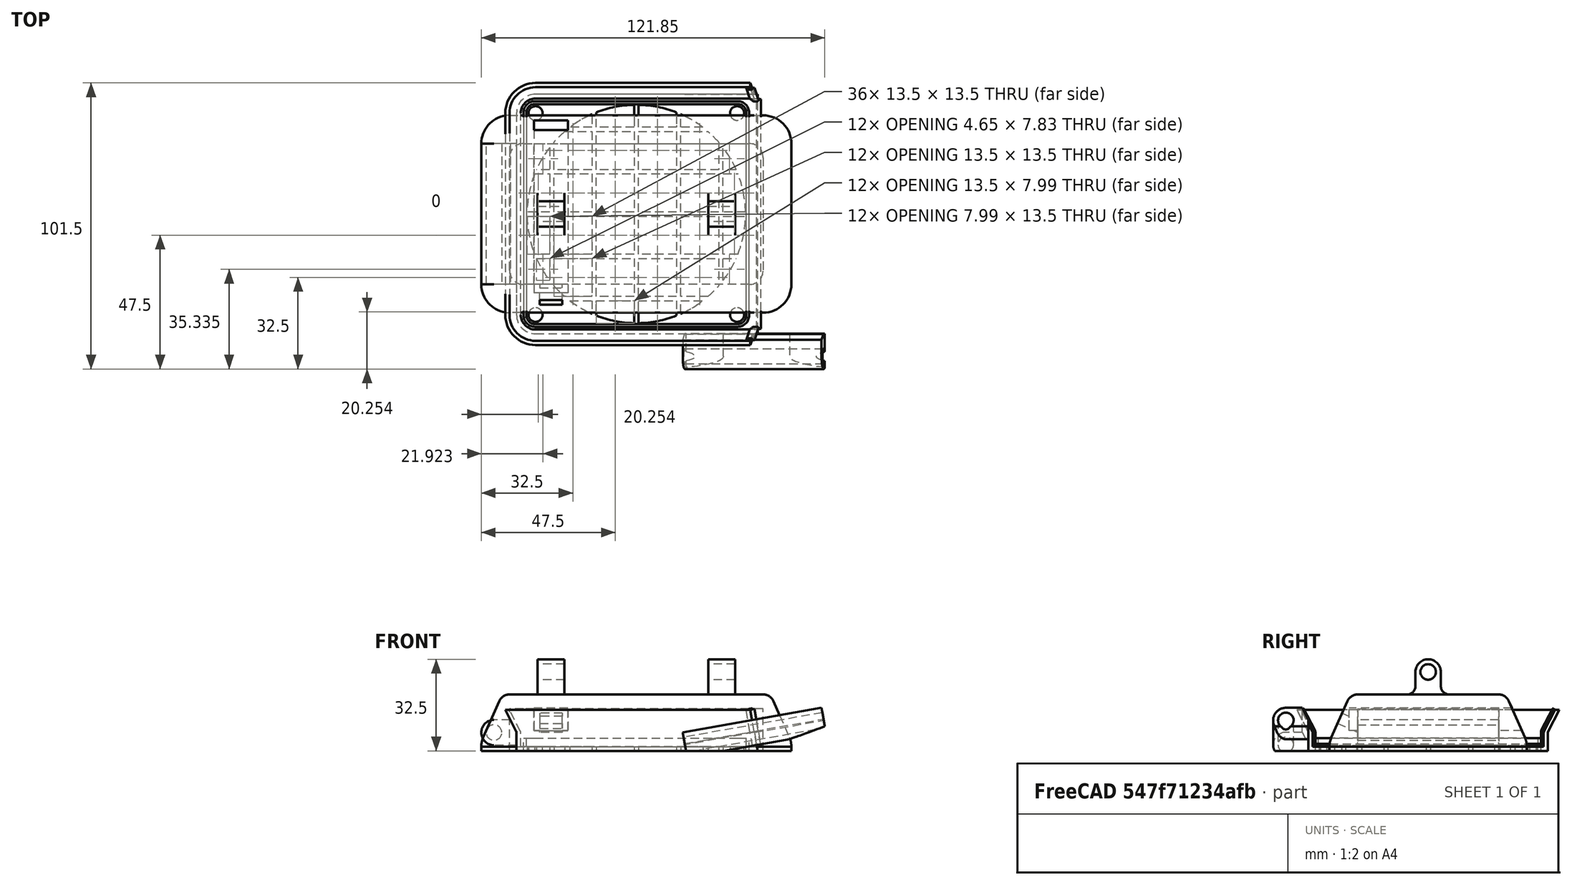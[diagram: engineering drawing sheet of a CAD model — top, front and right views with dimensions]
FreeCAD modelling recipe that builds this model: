
FCSTD DOCUMENT  (FreeCAD 1.0R39285 (Git))
Label: Solder Fume Extractor 2x80mm fans
License: All rights reserved
LicenseURL: https://en.wikipedia.org/wiki/All_rights_reserved
objects: Sketcher::SketchObject×29, PartDesign::Pad×17, PartDesign::CoordinateSystem×13, App::Link×10, PartDesign::Pocket×8, PartDesign::LinearPattern×6, PartDesign::Body×5, PartDesign::AdditivePipe×3, App::DocumentObjectGroup×3, App::FeaturePython×1, Mesh::Feature×1, PartDesign::SubtractivePipe×1, App::Part×1
note: 175 computed .brp shape members not serialized (recipe doc carries the construction recipe); baked Part::Feature solids carry a one-line shape summary decoded from their .brp
EXTERNAL_REF file=Axial Fan.FCStd obj=FanHouse_TopMountHole
EXTERNAL_REF file=Axial Fan.FCStd obj=Assembly

FEATURE [Sketcher::SketchObject] Sketch
  ArcFitTolerance = 1e-06
  AttachmentSupport = -> [XY_Plane]
  FullyConstrained = true
  MakeInternals = false
  MapMode = 5
  sketch-geometry (13):
    g0: LineSegment StartX=-42.5 StartY=35.75 StartZ=0 EndX=-42.5 EndY=-35.75 EndZ=0
    g1: LineSegment StartX=-35.75 StartY=-42.5 StartZ=0 EndX=60 EndY=-42.5 EndZ=0
    g2: LineSegment StartX=60 StartY=-42.5 StartZ=0 EndX=60 EndY=42.5 EndZ=0
    g3: LineSegment StartX=60 StartY=42.5 StartZ=0 EndX=-35.75 EndY=42.5 EndZ=0
    g4: Circle CenterX=-35.75 CenterY=35.75 CenterZ=0 NormalX=0 NormalY=0 NormalZ=1 AngleXU=0 Radius=2.5
    g5: Circle CenterX=35.75 CenterY=35.75 CenterZ=0 NormalX=0 NormalY=0 NormalZ=1 AngleXU=0 Radius=2.5
    g6: Circle CenterX=-35.75 CenterY=-35.75 CenterZ=0 NormalX=0 NormalY=0 NormalZ=1 AngleXU=0 Radius=2.5
    g7: Circle CenterX=35.75 CenterY=-35.75 CenterZ=0 NormalX=0 NormalY=0 NormalZ=1 AngleXU=0 Radius=2.5
    g8: Circle CenterX=0 CenterY=0 CenterZ=0 NormalX=0 NormalY=0 NormalZ=1 AngleXU=0 Radius=38.75
    g9: ArcOfCircle CenterX=-35.75 CenterY=35.75 CenterZ=0 NormalX=0 NormalY=0 NormalZ=1 AngleXU=0 Radius=6.75 StartAngle=1.5708 EndAngle=3.14159
    g10: GeomPoint [constr] X=-42.5 Y=42.5 Z=0
    g11: ArcOfCircle CenterX=-35.75 CenterY=-35.75 CenterZ=0 NormalX=0 NormalY=0 NormalZ=1 AngleXU=0 Radius=6.75 StartAngle=3.14159 EndAngle=4.71239
    g12: GeomPoint [constr] X=-42.5 Y=-42.5 Z=0
  constraints (30):
    c: Coincident(g1,g2)
    c: Coincident(g2,g3)
    c: Vertical(g2)
    c: Horizontal(g1)
    c: Horizontal(g3)
    c: DistanceY(g12,g10) = 85
    c: Equal(g7,g5)
    c: Equal(g5,g4)
    c: Equal(g4,g6)
    c: Diameter(g7) = 5
    c: Symmetric(g7,g5,g-1)
    c: Symmetric(g5,g4,g-2)
    c: Vertical(g6,g4)
    c: Horizontal(g6,g7)
    c: DistanceX(g4,g5) = 71.5
    c: DistanceY(g6,g4) = 71.5
    c: Symmetric(g12,g10,g-1)
    c: Coincident(g8,g-1)
    c: Diameter(g8) = 77.5
    c: DistanceX(g10,g-1) = 42.5
    c: DistanceX(g1) = 60
    c: PointOnObject(g10,g0)
    c: PointOnObject(g10,g3)
    c: Tangent(g0,g9) = -1.5708
    c: Tangent(g3,g9) = -1.5708
    c: PointOnObject(g12,g1)
    c: Tangent(g0,g11) = -1.5708
    c: Tangent(g1,g11) = -1.5708
    c: Equal(g11,g9)
    c: Coincident(g9,g4)
FEATURE [PartDesign::Pad] Pad
  Direction = (0,0,1)
  Length = 1.5
  Length2 = 10
  Profile = -> Sketch
  ReferenceAxis = -> Sketch [N_Axis]
  Refine = true
  Suppressed = false
  Type = 0
FEATURE [Sketcher::SketchObject] Sketch001
  ArcFitTolerance = 1e-06
  AttachmentSupport = -> [Pad]
  ExternalGeometry = -> [Pad]
  FullyConstrained = true
  MakeInternals = false
  MapMode = 5
  Placement = pos=(0,0,1.5) rot=(0,0,1;0rad)
  sketch-geometry (12):
    g0: LineSegment StartX=60 StartY=42.5 StartZ=0 EndX=-35.75 EndY=42.5 EndZ=0
    g1: LineSegment StartX=-42.5 StartY=35.75 StartZ=0 EndX=-42.5 EndY=-35.75 EndZ=0
    g2: LineSegment StartX=-35.75 StartY=-42.5 StartZ=0 EndX=60 EndY=-42.5 EndZ=0
    g3: ArcOfCircle CenterX=-35.75 CenterY=-35.75 CenterZ=0 NormalX=0 NormalY=0 NormalZ=1 AngleXU=0 Radius=6.75 StartAngle=3.14159 EndAngle=4.71239
    g4: ArcOfCircle CenterX=-35.75 CenterY=35.75 CenterZ=0 NormalX=0 NormalY=0 NormalZ=1 AngleXU=0 Radius=6.75 StartAngle=1.5708 EndAngle=3.14159
    g5: LineSegment StartX=60 StartY=-42.5 StartZ=0 EndX=60 EndY=-41 EndZ=0
    g6: LineSegment StartX=60 StartY=-41 StartZ=0 EndX=-35.75 EndY=-41 EndZ=0
    g7: LineSegment StartX=-41 StartY=-35.75 StartZ=0 EndX=-41 EndY=35.75 EndZ=0
    g8: LineSegment StartX=-35.75 StartY=41 StartZ=0 EndX=60 EndY=41 EndZ=0
    g9: LineSegment StartX=60 StartY=41 StartZ=0 EndX=60 EndY=42.5 EndZ=0
    g10: ArcOfCircle CenterX=-35.75 CenterY=-35.75 CenterZ=0 NormalX=0 NormalY=0 NormalZ=1 AngleXU=0 Radius=5.25 StartAngle=3.14159 EndAngle=4.71239
    g11: ArcOfCircle CenterX=-35.75 CenterY=35.75 CenterZ=0 NormalX=0 NormalY=0 NormalZ=1 AngleXU=0 Radius=5.25 StartAngle=1.5708 EndAngle=3.14159
  constraints (30):
    c: Coincident(g0,g-3)
    c: Coincident(g0,g-4)
    c: Horizontal(g2)
    c: Symmetric(g2,g0,g-1)
    c: Equal(g2,g0)
    c: Coincident(g-5,g1)
    c: Coincident(g1,g-5)
    c: Coincident(g3,g2)
    c: Coincident(g3,g1)
    c: Coincident(g4,g1)
    c: Coincident(g4,g0)
    c: Equal(g4,g-4)
    c: Equal(g-4,g3)
    c: Coincident(g5,g2)
    c: Vertical(g5)
    c: Coincident(g6,g5)
    c: Horizontal(g6)
    c: Vertical(g7)
    c: Coincident(g9,g8)
    c: Coincident(g9,g0)
    c: Horizontal(g8)
    c: Vertical(g9)
    c: Equal(g5,g9)
    c: Equal(g6,g8)
    c: Tangent(g10,g6) = 1.5708
    c: Tangent(g10,g7) = 1.5708
    c: Tangent(g11,g7) = 1.5708
    c: Tangent(g11,g8) = 1.5708
    c: DistanceY(g5,g5) = 1.5
    c: Coincident(g11,g4)
FEATURE [PartDesign::Pad] Pad001
  BaseFeature = -> Pad
  Direction = (0,0,1)
  Length = 5
  Length2 = 10
  Profile = -> Sketch001
  ReferenceAxis = -> Sketch001 [N_Axis]
  Refine = true
  Suppressed = false
  Type = 0
FEATURE [Sketcher::SketchObject] Sketch002
  ArcFitTolerance = 1e-06
  AttachmentSupport = -> [Pad001]
  ExternalGeometry = -> [Pad001]
  FullyConstrained = true
  MakeInternals = false
  MapMode = 5
  Placement = pos=(60,0,0) rot=(0.57735,0.57735,0.57735;2.0944rad)
  sketch-geometry (6):
    g0: LineSegment StartX=41.1112 StartY=6.9583 StartZ=0 EndX=45 EndY=14.5 EndZ=0
    g1: LineSegment StartX=45 StartY=14.5 StartZ=0 EndX=46.5 EndY=14.5 EndZ=0
    g2: LineSegment StartX=46.5 StartY=14.5 StartZ=0 EndX=42.6112 EndY=6.9583 EndZ=0
    g3: ArcOfCircle CenterX=43.5 CenterY=6.5 CenterZ=0 NormalX=0 NormalY=0 NormalZ=1 AngleXU=0 Radius=1 StartAngle=2.66551 EndAngle=3.14159
    g4: ArcOfCircle CenterX=42 CenterY=6.5 CenterZ=0 NormalX=0 NormalY=0 NormalZ=1 AngleXU=0 Radius=1 StartAngle=2.66551 EndAngle=3.14159
    g5: LineSegment StartX=42.5 StartY=6.5 StartZ=0 EndX=41 EndY=6.5 EndZ=0
  constraints (16):
    c: Coincident(g0,g1)
    c: Horizontal(g1)
    c: Coincident(g1,g2)
    c: Coincident(g3,g-3)
    c: Coincident(g4,g-3)
    c: Tangent(g4,g0) = 1.5708
    c: Tangent(g3,g2) = -1.5708
    c: Coincident(g5,g3)
    c: Coincident(g5,g4)
    c: Perpendicular(g3,g5)
    c: Perpendicular(g4,g5)
    c: Equal(g1,g5)
    c: Radius(g4) = 1
    c: DistanceY(g3,g1) = 8
    c: DistanceX(g3,g1) = 4
    c: Equal(g4,g3)
FEATURE [PartDesign::AdditivePipe] AdditivePipe
  AuxilleryCurvelinear = true
  AuxillerySpineTangent = false
  BaseFeature = -> Pad001
  Binormal = (0,0,0)
  Mode = 0
  Profile = -> Sketch002
  Refine = true
  Spine = -> Pad001 [Edge32,Edge33,Edge34,Edge35,Edge36]
  SpineTangent = false
  Suppressed = false
  Transformation = 0
  Transition = 0
FEATURE [Sketcher::SketchObject] Sketch003
  ArcFitTolerance = 1e-06
  AttachmentSupport = -> [XY_Plane]
  ExternalGeometry = -> [AdditivePipe]
  FullyConstrained = true
  MakeInternals = false
  MapMode = 5
  sketch-geometry (5):
    g0: LineSegment StartX=-30.75 StartY=42.5 StartZ=0 EndX=-30.75 EndY=-42.5 EndZ=0
    g1: LineSegment StartX=-30.75 StartY=-42.5 StartZ=0 EndX=-29.25 EndY=-42.5 EndZ=0
    g2: LineSegment StartX=-29.25 StartY=-42.5 StartZ=0 EndX=-29.25 EndY=42.5 EndZ=0
    g3: LineSegment StartX=-29.25 StartY=42.5 StartZ=0 EndX=-30.75 EndY=42.5 EndZ=0
    g4: GeomPoint [constr] X=-30 Y=0 Z=0
  constraints (13):
    c: Coincident(g0,g1)
    c: Coincident(g1,g2)
    c: Coincident(g2,g3)
    c: Coincident(g3,g0)
    c: Vertical(g0)
    c: Vertical(g2)
    c: Horizontal(g1)
    c: Horizontal(g3)
    c: Symmetric(g2,g0,g4)
    c: PointOnObject(g4,g-1)
    c: PointOnObject(g1,g-3)
    c: DistanceX(g3,g3) = 1.5
    c: DistanceX(g4,g-1) = 30
FEATURE [PartDesign::Pad] Pad002
  BaseFeature = -> AdditivePipe
  Direction = (0,0,1)
  Length = 10
  Length2 = 10
  Profile = -> Sketch003
  ReferenceAxis = -> Sketch003 [N_Axis]
  Refine = true
  Suppressed = false
  Type = 3
  UpToFace = -> AdditivePipe [Face2]
FEATURE [PartDesign::LinearPattern] LinearPattern
  BaseFeature = -> Pad002
  Direction = -> Sketch003 [H_Axis]
  Length = 60
  Mode = 0
  Occurrences = 5
  Offset = 15
  Originals = -> [Pad002]
  Refine = true
  Suppressed = false
  TransformMode = 0
FEATURE [Sketcher::SketchObject] Sketch004
  ArcFitTolerance = 1e-06
  AttachmentSupport = -> [XY_Plane]
  ExternalGeometry = -> [LinearPattern]
  FullyConstrained = true
  MakeInternals = false
  MapMode = 5
  sketch-geometry (5):
    g0: LineSegment StartX=42.5 StartY=29.25 StartZ=0 EndX=42.5 EndY=30.75 EndZ=0
    g1: LineSegment StartX=42.5 StartY=30.75 StartZ=0 EndX=-42.5 EndY=30.75 EndZ=0
    g2: LineSegment StartX=-42.5 StartY=30.75 StartZ=0 EndX=-42.5 EndY=29.25 EndZ=0
    g3: LineSegment StartX=-42.5 StartY=29.25 StartZ=0 EndX=42.5 EndY=29.25 EndZ=0
    g4: GeomPoint [constr] X=0 Y=30 Z=0
  constraints (13):
    c: Coincident(g0,g1)
    c: Coincident(g1,g2)
    c: Coincident(g2,g3)
    c: Coincident(g3,g0)
    c: Vertical(g0)
    c: Vertical(g2)
    c: Horizontal(g1)
    c: Horizontal(g3)
    c: Symmetric(g2,g0,g4)
    c: PointOnObject(g4,g-2)
    c: PointOnObject(g1,g-3)
    c: DistanceY(g4) = 30
    c: DistanceY(g0,g0) = 1.5
FEATURE [PartDesign::Pad] Pad003
  BaseFeature = -> LinearPattern
  Direction = (0,0,1)
  Length = 10
  Length2 = 10
  Profile = -> Sketch004
  ReferenceAxis = -> Sketch004 [N_Axis]
  Refine = true
  Suppressed = false
  Type = 3
  UpToFace = -> LinearPattern [Face31]
FEATURE [PartDesign::LinearPattern] LinearPattern001
  BaseFeature = -> Pad003
  Direction = -> Sketch004 [V_Axis]
  Length = 60
  Mode = 0
  Occurrences = 5
  Offset = 15
  Originals = -> [Pad003]
  Refine = true
  Reversed = true
  Suppressed = false
  TransformMode = 0
FEATURE [PartDesign::CoordinateSystem] FanMountHole
  AttacherType = Attacher::AttachEngine3D
  AttachmentSupport = -> [LinearPattern001]
  MapMode = 11
  Placement = pos=(-35.75,-35.75,0) rot=(0,0,1;1.5708rad)
FEATURE [PartDesign::CoordinateSystem] LCS_Origin
  AttacherType = Attacher::AttachEngine3D
  AttachmentSupport = -> [X_Axis001]
  MapMode = 2
FEATURE [App::DocumentObjectGroup] Constraints
FEATURE [App::FeaturePython] Variables  # WARN: FeaturePython — macro-defined, semantics opaque (R4)
  Type = App::PropertyContainer
FEATURE [App::DocumentObjectGroup] Configurations
FEATURE [Sketcher::SketchObject] Sketch005
  ArcFitTolerance = 1e-06
  AttachmentSupport = -> [XZ_Plane]
  ExternalGeometry = -> [LinearPattern001]
  FullyConstrained = true
  MakeInternals = false
  MapMode = 5
  Placement = pos=(0,0,0) rot=(1,0,0;1.5708rad)
  sketch-geometry (4):
    g0: LineSegment StartX=60 StartY=14.5 StartZ=0 EndX=60 EndY=0 EndZ=0
    g1: LineSegment StartX=60 StartY=0 StartZ=0 EndX=43 EndY=0 EndZ=0
    g2: LineSegment StartX=43 StartY=0 StartZ=0 EndX=40.4433 EndY=14.5 EndZ=0
    g3: LineSegment StartX=40.4433 StartY=14.5 StartZ=0 EndX=60 EndY=14.5 EndZ=0
  constraints (11):
    c: Coincident(g-3,g0)
    c: PointOnObject(g0,g-1)
    c: Vertical(g0)
    c: Coincident(g0,g1)
    c: PointOnObject(g1,g-1)
    c: Coincident(g1,g2)
    c: PointOnObject(g2,g-3)
    c: Coincident(g2,g3)
    c: Coincident(g3,g0)
    c: DistanceX(g-1,g1) = 43
    c: Angle(g1,g2) = 1.74533
FEATURE [PartDesign::Pocket] Pocket
  BaseFeature = -> LinearPattern001
  Direction = (0,1,-2e-16)
  Length = 5
  Length2 = 5
  Midplane = true
  Profile = -> Sketch005
  ReferenceAxis = -> Sketch005 [N_Axis]
  Refine = true
  Suppressed = false
  Type = 1
FEATURE [PartDesign::CoordinateSystem] OtherFanHolder
  AttacherType = Attacher::AttachEngine3D
  AttachmentSupport = -> [Pocket]
  MapMode = 45
  Placement = pos=(42.8701,0,0.736527) rot=(0.642788,0,0.766044;3.14159rad)
FEATURE [PartDesign::CoordinateSystem] FilterHolderMount
  AttacherType = Attacher::AttachEngine3D
  AttachmentSupport = -> [Pocket]
  MapMode = 11
  Placement = pos=(-35.75,35.75,1.5) rot=(0,0,1;1.5708rad)
FEATURE [Sketcher::SketchObject] Sketch006
  ArcFitTolerance = 1e-06
  AttachmentSupport = -> [XY_Plane002]
  FullyConstrained = true
  MakeInternals = false
  MapMode = 5
  sketch-geometry (15):
    g0: LineSegment StartX=40 StartY=-36 StartZ=0 EndX=40 EndY=36 EndZ=0
    g1: LineSegment StartX=36 StartY=40 StartZ=0 EndX=-36 EndY=40 EndZ=0
    g2: LineSegment StartX=-40 StartY=36 StartZ=0 EndX=-40 EndY=-36 EndZ=0
    g3: LineSegment StartX=-36 StartY=-40 StartZ=0 EndX=36 EndY=-40 EndZ=0
    g4: ArcOfCircle CenterX=36 CenterY=-36 CenterZ=0 NormalX=0 NormalY=0 NormalZ=1 AngleXU=0 Radius=4 StartAngle=4.71239 EndAngle=6.28319
    g5: ArcOfCircle CenterX=36 CenterY=36 CenterZ=0 NormalX=0 NormalY=0 NormalZ=1 AngleXU=0 Radius=4 StartAngle=2e-16 EndAngle=1.5708
    g6: ArcOfCircle CenterX=-36 CenterY=36 CenterZ=0 NormalX=0 NormalY=0 NormalZ=1 AngleXU=0 Radius=4 StartAngle=1.5708 EndAngle=3.14159
    g7: ArcOfCircle CenterX=-36 CenterY=-36 CenterZ=0 NormalX=0 NormalY=0 NormalZ=1 AngleXU=0 Radius=4 StartAngle=3.14159 EndAngle=4.71239
    g8: GeomPoint [constr] X=40 Y=-40 Z=0
    g9: GeomPoint [constr] X=-40 Y=40 Z=0
    g10: Circle CenterX=-35.75 CenterY=35.75 CenterZ=0 NormalX=0 NormalY=0 NormalZ=1 AngleXU=0 Radius=2.5
    g11: Circle CenterX=35.75 CenterY=35.75 CenterZ=0 NormalX=0 NormalY=0 NormalZ=1 AngleXU=0 Radius=2.5
    g12: Circle CenterX=35.75 CenterY=-35.75 CenterZ=0 NormalX=0 NormalY=0 NormalZ=1 AngleXU=0 Radius=2.5
    g13: Circle CenterX=-35.75 CenterY=-35.75 CenterZ=0 NormalX=0 NormalY=0 NormalZ=1 AngleXU=0 Radius=2.5
    g14: Circle CenterX=0 CenterY=0 CenterZ=0 NormalX=0 NormalY=0 NormalZ=1 AngleXU=0 Radius=38.75
  constraints (34):
    c: Tangent(g0,g4) = -1.5708
    c: Tangent(g0,g5) = -1.5708
    c: Tangent(g1,g5) = -1.5708
    c: Tangent(g1,g6) = -1.5708
    c: Tangent(g2,g6) = -1.5708
    c: Tangent(g2,g7) = -1.5708
    c: Tangent(g3,g7) = -1.5708
    c: Tangent(g3,g4) = -1.5708
    c: Vertical(g2)
    c: Horizontal(g1)
    c: Equal(g4,g5)
    c: Equal(g5,g6)
    c: Equal(g6,g7)
    c: PointOnObject(g8,g0)
    c: PointOnObject(g8,g3)
    c: PointOnObject(g9,g1)
    c: PointOnObject(g9,g2)
    c: Radius(g7) = 4
    c: Symmetric(g3,g3,g-2)
    c: Symmetric(g0,g0,g-1)
    c: Equal(g0,g3)
    c: DistanceY(g3,g1) = 80
    c: Equal(g10,g11)
    c: Equal(g11,g12)
    c: Equal(g12,g13)
    c: Symmetric(g10,g11,g-2)
    c: Symmetric(g11,g12,g-1)
    c: Horizontal(g12,g13)
    c: Vertical(g13,g10)
    c: DistanceY(g13,g10) = 71.5
    c: DistanceX(g10,g11) = 71.5
    c: Diameter(g11) = 5
    c: Coincident(g14,g-1)
    c: Diameter(g14) = 77.5
FEATURE [PartDesign::Pad] Pad004
  Direction = (0,0,1)
  Length = 1.5
  Length2 = 10
  Profile = -> Sketch006
  ReferenceAxis = -> Sketch006 [N_Axis]
  Refine = true
  Suppressed = false
  Type = 0
FEATURE [Sketcher::SketchObject] Sketch007
  ArcFitTolerance = 1e-06
  AttachmentSupport = -> [XY_Plane002]
  ExternalGeometry = -> [Pad004]
  FullyConstrained = true
  MakeInternals = false
  MapMode = 5
  sketch-geometry (5):
    g0: LineSegment StartX=-29.25 StartY=-40 StartZ=0 EndX=-29.25 EndY=40 EndZ=0
    g1: LineSegment StartX=-29.25 StartY=40 StartZ=0 EndX=-30.75 EndY=40 EndZ=0
    g2: LineSegment StartX=-30.75 StartY=40 StartZ=0 EndX=-30.75 EndY=-40 EndZ=0
    g3: LineSegment StartX=-30.75 StartY=-40 StartZ=0 EndX=-29.25 EndY=-40 EndZ=0
    g4: GeomPoint [constr] X=-30 Y=0 Z=0
  constraints (13):
    c: Coincident(g0,g1)
    c: Coincident(g1,g2)
    c: Coincident(g2,g3)
    c: Coincident(g3,g0)
    c: Vertical(g0)
    c: Vertical(g2)
    c: Horizontal(g1)
    c: Horizontal(g3)
    c: Symmetric(g2,g0,g4)
    c: PointOnObject(g4,g-1)
    c: PointOnObject(g1,g-3)
    c: DistanceX(g4,g-1) = 30
    c: DistanceX(g1,g1) = 1.5
FEATURE [PartDesign::Pad] Pad005
  BaseFeature = -> Pad004
  Direction = (0,0,1)
  Length = 10
  Length2 = 10
  Profile = -> Sketch007
  ReferenceAxis = -> Sketch007 [N_Axis]
  Refine = true
  Suppressed = false
  Type = 3
  UpToFace = -> Pad004 [Face15]
FEATURE [PartDesign::LinearPattern] LinearPattern002
  BaseFeature = -> Pad005
  Direction = -> Sketch007 [H_Axis]
  Length = 60
  Mode = 0
  Occurrences = 5
  Offset = 15
  Originals = -> [Pad005]
  Refine = true
  Suppressed = false
  TransformMode = 0
FEATURE [Sketcher::SketchObject] Sketch008
  ArcFitTolerance = 1e-06
  AttachmentSupport = -> [XY_Plane002]
  ExternalGeometry = -> [LinearPattern002]
  FullyConstrained = true
  MakeInternals = false
  MapMode = 5
  sketch-geometry (5):
    g0: LineSegment StartX=40 StartY=-30.75 StartZ=0 EndX=40 EndY=-29.25 EndZ=0
    g1: LineSegment StartX=40 StartY=-29.25 StartZ=0 EndX=-40 EndY=-29.25 EndZ=0
    g2: LineSegment StartX=-40 StartY=-29.25 StartZ=0 EndX=-40 EndY=-30.75 EndZ=0
    g3: LineSegment StartX=-40 StartY=-30.75 StartZ=0 EndX=40 EndY=-30.75 EndZ=0
    g4: GeomPoint [constr] X=0 Y=-30 Z=0
  constraints (13):
    c: Coincident(g0,g1)
    c: Coincident(g1,g2)
    c: Coincident(g2,g3)
    c: Coincident(g3,g0)
    c: Vertical(g0)
    c: Vertical(g2)
    c: Horizontal(g1)
    c: Horizontal(g3)
    c: Symmetric(g2,g0,g4)
    c: PointOnObject(g4,g-2)
    c: PointOnObject(g1,g-3)
    c: DistanceY(g4,g-1) = 30
    c: DistanceY(g0,g0) = 1.5
FEATURE [PartDesign::Pad] Pad006
  BaseFeature = -> LinearPattern002
  Direction = (0,0,1)
  Length = 10
  Length2 = 10
  Profile = -> Sketch008
  ReferenceAxis = -> Sketch008 [N_Axis]
  Refine = true
  Suppressed = false
  Type = 3
  UpToFace = -> LinearPattern002 [Face32]
FEATURE [PartDesign::LinearPattern] LinearPattern003
  BaseFeature = -> Pad006
  Direction = -> Sketch008 [V_Axis]
  Length = 60
  Mode = 0
  Occurrences = 5
  Offset = 15
  Originals = -> [Pad006]
  Refine = true
  Suppressed = false
  TransformMode = 0
FEATURE [Sketcher::SketchObject] Sketch009
  ArcFitTolerance = 1e-06
  AttachmentSupport = -> [LinearPattern003]
  ExternalGeometry = -> [LinearPattern003]
  FullyConstrained = true
  MakeInternals = false
  MapMode = 5
  Placement = pos=(0,0,1.5) rot=(0,0,1;0rad)
  sketch-geometry (20):
    g0: LineSegment StartX=-40 StartY=36 StartZ=0 EndX=-40 EndY=-36 EndZ=0
    g1: LineSegment StartX=-36 StartY=-40 StartZ=0 EndX=36 EndY=-40 EndZ=0
    g2: LineSegment StartX=40 StartY=-36 StartZ=0 EndX=40 EndY=36 EndZ=0
    g3: LineSegment StartX=36 StartY=40 StartZ=0 EndX=-36 EndY=40 EndZ=0
    g4: ArcOfCircle CenterX=-36 CenterY=36 CenterZ=0 NormalX=0 NormalY=0 NormalZ=1 AngleXU=0 Radius=4 StartAngle=1.5708 EndAngle=3.14159
    g5: ArcOfCircle CenterX=-36 CenterY=-36 CenterZ=0 NormalX=0 NormalY=0 NormalZ=1 AngleXU=0 Radius=4 StartAngle=3.14159 EndAngle=4.71239
    g6: ArcOfCircle CenterX=36 CenterY=-36 CenterZ=0 NormalX=0 NormalY=0 NormalZ=1 AngleXU=0 Radius=4 StartAngle=4.71239 EndAngle=6.28319
    g7: ArcOfCircle CenterX=36 CenterY=36 CenterZ=0 NormalX=0 NormalY=0 NormalZ=1 AngleXU=0 Radius=4 StartAngle=-9e-16 EndAngle=1.5708
    g8: GeomPoint [constr] X=-40 Y=40 Z=0
    g9: GeomPoint [constr] X=40 Y=-40 Z=0
    g10: LineSegment StartX=-39 StartY=36 StartZ=0 EndX=-39 EndY=-36 EndZ=0
    g11: LineSegment StartX=-36 StartY=-39 StartZ=0 EndX=36 EndY=-39 EndZ=0
    g12: LineSegment StartX=39 StartY=-36 StartZ=0 EndX=39 EndY=36 EndZ=0
    g13: LineSegment StartX=36 StartY=39 StartZ=0 EndX=-36 EndY=39 EndZ=0
    g14: ArcOfCircle CenterX=-36 CenterY=36 CenterZ=0 NormalX=0 NormalY=0 NormalZ=1 AngleXU=0 Radius=3 StartAngle=1.5708 EndAngle=3.14159
    g15: ArcOfCircle CenterX=-36 CenterY=-36 CenterZ=0 NormalX=0 NormalY=0 NormalZ=1 AngleXU=0 Radius=3 StartAngle=3.14159 EndAngle=4.71239
    g16: ArcOfCircle CenterX=36 CenterY=-36 CenterZ=0 NormalX=0 NormalY=0 NormalZ=1 AngleXU=0 Radius=3 StartAngle=4.71239 EndAngle=6.28319
    g17: ArcOfCircle CenterX=36 CenterY=36 CenterZ=0 NormalX=0 NormalY=0 NormalZ=1 AngleXU=0 Radius=3 StartAngle=-9e-16 EndAngle=1.5708
    g18: GeomPoint [constr] X=-39 Y=39 Z=0
    g19: GeomPoint [constr] X=39 Y=-39 Z=0
  constraints (44):
    c: Tangent(g0,g4) = -1.5708
    c: Tangent(g0,g5) = -1.5708
    c: Tangent(g1,g5) = -1.5708
    c: Tangent(g1,g6) = -1.5708
    c: Tangent(g2,g6) = -1.5708
    c: Tangent(g2,g7) = -1.5708
    c: Tangent(g3,g7) = -1.5708
    c: Tangent(g3,g4) = -1.5708
    c: Vertical(g0)
    c: Vertical(g2)
    c: Horizontal(g1)
    c: Equal(g4,g5)
    c: Equal(g5,g6)
    c: Equal(g6,g7)
    c: PointOnObject(g8,g0)
    c: PointOnObject(g8,g3)
    c: PointOnObject(g9,g1)
    c: PointOnObject(g9,g2)
    c: Coincident(g3,g-5)
    c: Equal(g-5,g7)
    c: Coincident(g3,g-3)
    c: Equal(g3,g2)
    c: Tangent(g10,g14) = -1.5708
    c: Tangent(g10,g15) = -1.5708
    c: Tangent(g11,g15) = -1.5708
    c: Tangent(g11,g16) = -1.5708
    c: Tangent(g12,g16) = -1.5708
    c: Tangent(g12,g17) = -1.5708
    c: Tangent(g13,g17) = -1.5708
    c: Tangent(g13,g14) = -1.5708
    c: Vertical(g10)
    c: Horizontal(g11)
    c: Equal(g14,g15)
    c: Equal(g15,g16)
    c: Equal(g16,g17)
    c: PointOnObject(g18,g10)
    c: PointOnObject(g18,g13)
    c: PointOnObject(g19,g11)
    c: PointOnObject(g19,g12)
    c: Symmetric(g12,g12,g-1)
    c: Symmetric(g13,g13,g-2)
    c: Equal(g11,g12)
    c: DistanceX(g12,g2) = 1
    c: Horizontal(g2,g12)
FEATURE [PartDesign::Pad] Pad007
  BaseFeature = -> LinearPattern003
  Direction = (0,0,1)
  Length = 3
  Length2 = 10
  Profile = -> Sketch009
  ReferenceAxis = -> Sketch009 [N_Axis]
  Refine = true
  Suppressed = false
  Type = 0
FEATURE [PartDesign::CoordinateSystem] FanHolder
  AttacherType = Attacher::AttachEngine3D
  AttachmentOffset = pos=(0,0,3) rot=(0,0,1;0rad)
  AttachmentSupport = -> [Pad007]
  MapMode = 11
  Placement = pos=(-35.75,35.75,4.5) rot=(0,0,1;1.5708rad)
FEATURE [PartDesign::Body] Body001  label="FilterHolder"
  AllowCompound = false
  Group = -> [Sketch006,Pad004,Sketch007,Pad005,LinearPattern002,Sketch008,Pad006,LinearPattern003,Sketch009,Pad007,FanHolder]
  Origin = -> Origin002
  Tip = -> Pad007
FEATURE [Sketcher::SketchObject] Sketch010
  ArcFitTolerance = 1e-06
  AttachmentSupport = -> [XZ_Plane]
  ExternalGeometry = -> [Pocket]
  FullyConstrained = true
  MakeInternals = false
  MapMode = 5
  Placement = pos=(0,0,0) rot=(1,0,0;1.5708rad)
  sketch-geometry (7):
    g0: ArcOfCircle CenterX=-43.5 CenterY=6.5 CenterZ=0 NormalX=0 NormalY=0 NormalZ=1 AngleXU=0 Radius=1 StartAngle=-2.4e-14 EndAngle=0.476081
    g1: LineSegment StartX=-42.5 StartY=6.5 StartZ=0 EndX=-42.5 EndY=2 EndZ=0
    g2: LineSegment StartX=-42.5 StartY=2 StartZ=0 EndX=-50.5 EndY=2 EndZ=0
    g3: LineSegment StartX=-42.6112 StartY=6.9583 StartZ=0 EndX=-44.6953 EndY=11 EndZ=0
    g4: LineSegment StartX=-44.6953 StartY=11 StartZ=0 EndX=-50.5 EndY=11 EndZ=0
    g5: ArcOfCircle CenterX=-50.5 CenterY=6.5 CenterZ=0 NormalX=0 NormalY=0 NormalZ=1 AngleXU=0 Radius=4.5 StartAngle=1.5708 EndAngle=4.71239
    g6: Circle CenterX=-50.5 CenterY=6.5 CenterZ=0 NormalX=0 NormalY=0 NormalZ=1 AngleXU=0 Radius=2.75
  constraints (18):
    c: Coincident(g0,g-5)
    c: Coincident(g0,g-5)
    c: Equal(g-5,g0)
    c: Coincident(g1,g0)
    c: PointOnObject(g1,g-3)
    c: Coincident(g2,g1)
    c: Horizontal(g2)
    c: Coincident(g3,g0)
    c: PointOnObject(g3,g-4)
    c: Horizontal(g4)
    c: Tangent(g5,g4) = -1.5708
    c: Tangent(g5,g2) = 1.5708
    c: Diameter(g5) = 9
    c: Diameter(g6) = 5.5
    c: Coincident(g6,g5)
    c: Horizontal(g0,g5)
    c: Coincident(g3,g4)
    c: DistanceX(g5,g-4) = 4
FEATURE [PartDesign::Pad] Pad008
  BaseFeature = -> Pocket
  Direction = (0,-1,2e-16)
  Length = 50
  Length2 = 10
  Midplane = true
  Profile = -> Sketch010
  ReferenceAxis = -> Sketch010 [N_Axis]
  Refine = true
  Suppressed = false
  Type = 0
FEATURE [Sketcher::SketchObject] Sketch011
  ArcFitTolerance = 1e-06
  AttachmentSupport = -> [Pad008]
  ExternalGeometry = -> [Pad008]
  FullyConstrained = true
  MakeInternals = false
  MapMode = 5
  Placement = pos=(41.7034,1.6e-15,7.35343) rot=(0.540716,0.540716,0.6444;1.99673rad)
  sketch-geometry (7):
    g0: ArcOfCircle CenterX=-43.0908 CenterY=-0.761797 CenterZ=0 NormalX=0 NormalY=0 NormalZ=1 AngleXU=0 Radius=0.6 StartAngle=6.10761 EndAngle=6.92787
    g1: LineSegment StartX=-44.66 StartY=3.6334 StartZ=0 EndX=-42.6112 EndY=-0.401229 EndZ=0
    g2: LineSegment StartX=-42.5 StartY=-5.3666 StartZ=0 EndX=-42.5 EndY=-0.866599 EndZ=0
    g3: LineSegment StartX=-42.5 StartY=-5.3666 StartZ=0 EndX=-50.5 EndY=-5.3666 EndZ=0
    g4: LineSegment StartX=-44.66 StartY=3.6334 StartZ=0 EndX=-50.5 EndY=3.6334 EndZ=0
    g5: ArcOfCircle CenterX=-50.5 CenterY=-0.866599 CenterZ=0 NormalX=0 NormalY=0 NormalZ=1 AngleXU=0 Radius=4.5 StartAngle=1.5708 EndAngle=4.71239
    g6: Circle CenterX=-50.5 CenterY=-0.866599 CenterZ=0 NormalX=0 NormalY=0 NormalZ=1 AngleXU=0 Radius=2.75
  constraints (18):
    c: Coincident(g0,g-3)
    c: Coincident(g0,g-4)
    c: Radius(g0) = 0.6
    c: Coincident(g3,g2)
    c: Horizontal(g3)
    c: Coincident(g4,g1)
    c: Horizontal(g4)
    c: Tangent(g5,g4) = -1.5708
    c: Tangent(g5,g3) = 1.5708
    c: Diameter(g5) = 9
    c: Horizontal(g5,g2)
    c: Coincident(g6,g5)
    c: Diameter(g6) = 5.5
    c: DistanceX(g5,g-4) = 4
    c: Coincident(g2,g0)
    c: PointOnObject(g1,g-4)
    c: PointOnObject(g2,g-3)
    c: Coincident(g0,g1)
FEATURE [PartDesign::Pad] Pad009
  BaseFeature = -> Pad008
  Direction = (0.984808,-2e-16,0.173648)
  Length = 50
  Length2 = 10
  Midplane = true
  Profile = -> Sketch011
  ReferenceAxis = -> Sketch011 [N_Axis]
  Refine = true
  Suppressed = false
  Type = 0
FEATURE [Mesh::Feature] base_mount
FEATURE [Sketcher::SketchObject] Sketch014
  ArcFitTolerance = 1e-06
  AttachmentSupport = -> [XY_Plane004]
  FullyConstrained = true
  MakeInternals = false
  MapMode = 5
  sketch-geometry (13):
    g0: LineSegment StartX=-42.5 StartY=35.75 StartZ=0 EndX=-42.5 EndY=-35.75 EndZ=0
    g1: LineSegment StartX=-35.75 StartY=-42.5 StartZ=0 EndX=60 EndY=-42.5 EndZ=0
    g2: LineSegment StartX=60 StartY=-42.5 StartZ=0 EndX=60 EndY=42.5 EndZ=0
    g3: LineSegment StartX=60 StartY=42.5 StartZ=0 EndX=-35.75 EndY=42.5 EndZ=0
    g4: Circle CenterX=-35.75 CenterY=35.75 CenterZ=0 NormalX=0 NormalY=0 NormalZ=1 AngleXU=0 Radius=2.5
    g5: Circle CenterX=35.75 CenterY=35.75 CenterZ=0 NormalX=0 NormalY=0 NormalZ=1 AngleXU=0 Radius=2.5
    g6: Circle CenterX=-35.75 CenterY=-35.75 CenterZ=0 NormalX=0 NormalY=0 NormalZ=1 AngleXU=0 Radius=2.5
    g7: Circle CenterX=35.75 CenterY=-35.75 CenterZ=0 NormalX=0 NormalY=0 NormalZ=1 AngleXU=0 Radius=2.5
    g8: Circle CenterX=0 CenterY=0 CenterZ=0 NormalX=0 NormalY=0 NormalZ=1 AngleXU=0 Radius=38.75
    g9: ArcOfCircle CenterX=-35.75 CenterY=35.75 CenterZ=0 NormalX=0 NormalY=0 NormalZ=1 AngleXU=0 Radius=6.75 StartAngle=1.5708 EndAngle=3.14159
    g10: GeomPoint [constr] X=-42.5 Y=42.5 Z=0
    g11: ArcOfCircle CenterX=-35.75 CenterY=-35.75 CenterZ=0 NormalX=0 NormalY=0 NormalZ=1 AngleXU=0 Radius=6.75 StartAngle=3.14159 EndAngle=4.71239
    g12: GeomPoint [constr] X=-42.5 Y=-42.5 Z=0
  constraints (30):
    c: Coincident(g1,g2)
    c: Coincident(g2,g3)
    c: Vertical(g2)
    c: Horizontal(g1)
    c: Horizontal(g3)
    c: DistanceY(g12,g10) = 85
    c: Equal(g7,g5)
    c: Equal(g5,g4)
    c: Equal(g4,g6)
    c: Diameter(g7) = 5
    c: Symmetric(g7,g5,g-1)
    c: Symmetric(g5,g4,g-2)
    c: Vertical(g6,g4)
    c: Horizontal(g6,g7)
    c: DistanceX(g4,g5) = 71.5
    c: DistanceY(g6,g4) = 71.5
    c: Symmetric(g12,g10,g-1)
    c: Coincident(g8,g-1)
    c: Diameter(g8) = 77.5
    c: DistanceX(g10,g-1) = 42.5
    c: DistanceX(g1) = 60
    c: PointOnObject(g10,g0)
    c: PointOnObject(g10,g3)
    c: Tangent(g0,g9) = -1.5708
    c: Tangent(g3,g9) = -1.5708
    c: PointOnObject(g12,g1)
    c: Tangent(g0,g11) = -1.5708
    c: Tangent(g1,g11) = -1.5708
    c: Equal(g11,g9)
    c: Coincident(g9,g4)
FEATURE [PartDesign::Pad] Pad010
  Direction = (0,0,1)
  Length = 1.5
  Length2 = 10
  Profile = -> Sketch014
  ReferenceAxis = -> Sketch014 [N_Axis]
  Refine = true
  Suppressed = false
  Type = 0
FEATURE [Sketcher::SketchObject] Sketch015
  ArcFitTolerance = 1e-06
  AttachmentSupport = -> [Pad010]
  ExternalGeometry = -> [Pad010]
  FullyConstrained = true
  MakeInternals = false
  MapMode = 5
  Placement = pos=(0,0,1.5) rot=(0,0,1;0rad)
  sketch-geometry (12):
    g0: LineSegment StartX=60 StartY=42.5 StartZ=0 EndX=-35.75 EndY=42.5 EndZ=0
    g1: LineSegment StartX=-42.5 StartY=35.75 StartZ=0 EndX=-42.5 EndY=-35.75 EndZ=0
    g2: LineSegment StartX=-35.75 StartY=-42.5 StartZ=0 EndX=60 EndY=-42.5 EndZ=0
    g3: ArcOfCircle CenterX=-35.75 CenterY=-35.75 CenterZ=0 NormalX=0 NormalY=0 NormalZ=1 AngleXU=0 Radius=6.75 StartAngle=3.14159 EndAngle=4.71239
    g4: ArcOfCircle CenterX=-35.75 CenterY=35.75 CenterZ=0 NormalX=0 NormalY=0 NormalZ=1 AngleXU=0 Radius=6.75 StartAngle=1.5708 EndAngle=3.14159
    g5: LineSegment StartX=60 StartY=-42.5 StartZ=0 EndX=60 EndY=-41 EndZ=0
    g6: LineSegment StartX=60 StartY=-41 StartZ=0 EndX=-35.75 EndY=-41 EndZ=0
    g7: LineSegment StartX=-41 StartY=-35.75 StartZ=0 EndX=-41 EndY=35.75 EndZ=0
    g8: LineSegment StartX=-35.75 StartY=41 StartZ=0 EndX=60 EndY=41 EndZ=0
    g9: LineSegment StartX=60 StartY=41 StartZ=0 EndX=60 EndY=42.5 EndZ=0
    g10: ArcOfCircle CenterX=-35.75 CenterY=-35.75 CenterZ=0 NormalX=0 NormalY=0 NormalZ=1 AngleXU=0 Radius=5.25 StartAngle=3.14159 EndAngle=4.71239
    g11: ArcOfCircle CenterX=-35.75 CenterY=35.75 CenterZ=0 NormalX=0 NormalY=0 NormalZ=1 AngleXU=0 Radius=5.25 StartAngle=1.5708 EndAngle=3.14159
  constraints (30):
    c: Coincident(g0,g-3)
    c: Coincident(g0,g-4)
    c: Horizontal(g2)
    c: Symmetric(g2,g0,g-1)
    c: Equal(g2,g0)
    c: Coincident(g-5,g1)
    c: Coincident(g1,g-5)
    c: Coincident(g3,g2)
    c: Coincident(g3,g1)
    c: Coincident(g4,g1)
    c: Coincident(g4,g0)
    c: Equal(g4,g-4)
    c: Equal(g-4,g3)
    c: Coincident(g5,g2)
    c: Vertical(g5)
    c: Coincident(g6,g5)
    c: Horizontal(g6)
    c: Vertical(g7)
    c: Coincident(g9,g8)
    c: Coincident(g9,g0)
    c: Horizontal(g8)
    c: Vertical(g9)
    c: Equal(g5,g9)
    c: Equal(g6,g8)
    c: Tangent(g10,g6) = 1.5708
    c: Tangent(g10,g7) = 1.5708
    c: Tangent(g11,g7) = 1.5708
    c: Tangent(g11,g8) = 1.5708
    c: DistanceY(g5,g5) = 1.5
    c: Coincident(g11,g4)
FEATURE [PartDesign::Pad] Pad011
  BaseFeature = -> Pad010
  Direction = (0,0,1)
  Length = 5
  Length2 = 10
  Profile = -> Sketch015
  ReferenceAxis = -> Sketch015 [N_Axis]
  Refine = true
  Suppressed = false
  Type = 0
FEATURE [Sketcher::SketchObject] Sketch016
  ArcFitTolerance = 1e-06
  AttachmentSupport = -> [Pad011]
  ExternalGeometry = -> [Pad011]
  FullyConstrained = true
  MakeInternals = false
  MapMode = 5
  Placement = pos=(60,0,0) rot=(0.57735,0.57735,0.57735;2.0944rad)
  sketch-geometry (6):
    g0: LineSegment StartX=41.1112 StartY=6.9583 StartZ=0 EndX=45 EndY=14.5 EndZ=0
    g1: LineSegment StartX=45 StartY=14.5 StartZ=0 EndX=46.5 EndY=14.5 EndZ=0
    g2: LineSegment StartX=46.5 StartY=14.5 StartZ=0 EndX=42.6112 EndY=6.9583 EndZ=0
    g3: ArcOfCircle CenterX=43.5 CenterY=6.5 CenterZ=0 NormalX=0 NormalY=0 NormalZ=1 AngleXU=0 Radius=1 StartAngle=2.66551 EndAngle=3.14159
    g4: ArcOfCircle CenterX=42 CenterY=6.5 CenterZ=0 NormalX=0 NormalY=0 NormalZ=1 AngleXU=0 Radius=1 StartAngle=2.66551 EndAngle=3.14159
    g5: LineSegment StartX=42.5 StartY=6.5 StartZ=0 EndX=41 EndY=6.5 EndZ=0
  constraints (16):
    c: Coincident(g0,g1)
    c: Horizontal(g1)
    c: Coincident(g1,g2)
    c: Coincident(g3,g-3)
    c: Coincident(g4,g-3)
    c: Tangent(g4,g0) = 1.5708
    c: Tangent(g3,g2) = -1.5708
    c: Coincident(g5,g3)
    c: Coincident(g5,g4)
    c: Perpendicular(g3,g5)
    c: Perpendicular(g4,g5)
    c: Equal(g1,g5)
    c: Radius(g4) = 1
    c: DistanceY(g3,g1) = 8
    c: DistanceX(g3,g1) = 4
    c: Equal(g4,g3)
FEATURE [PartDesign::AdditivePipe] AdditivePipe001
  AuxilleryCurvelinear = true
  AuxillerySpineTangent = false
  BaseFeature = -> Pad011
  Binormal = (0,0,0)
  Mode = 0
  Profile = -> Sketch016
  Refine = true
  Spine = -> Pad011 [Edge32,Edge33,Edge34,Edge35,Edge36]
  SpineTangent = false
  Suppressed = false
  Transformation = 0
  Transition = 0
FEATURE [Sketcher::SketchObject] Sketch017
  ArcFitTolerance = 1e-06
  AttachmentSupport = -> [XY_Plane004]
  ExternalGeometry = -> [AdditivePipe001]
  FullyConstrained = true
  MakeInternals = false
  MapMode = 5
  sketch-geometry (5):
    g0: LineSegment StartX=-30.75 StartY=42.5 StartZ=0 EndX=-30.75 EndY=-42.5 EndZ=0
    g1: LineSegment StartX=-30.75 StartY=-42.5 StartZ=0 EndX=-29.25 EndY=-42.5 EndZ=0
    g2: LineSegment StartX=-29.25 StartY=-42.5 StartZ=0 EndX=-29.25 EndY=42.5 EndZ=0
    g3: LineSegment StartX=-29.25 StartY=42.5 StartZ=0 EndX=-30.75 EndY=42.5 EndZ=0
    g4: GeomPoint [constr] X=-30 Y=0 Z=0
  constraints (13):
    c: Coincident(g0,g1)
    c: Coincident(g1,g2)
    c: Coincident(g2,g3)
    c: Coincident(g3,g0)
    c: Vertical(g0)
    c: Vertical(g2)
    c: Horizontal(g1)
    c: Horizontal(g3)
    c: Symmetric(g2,g0,g4)
    c: PointOnObject(g4,g-1)
    c: PointOnObject(g1,g-3)
    c: DistanceX(g3,g3) = 1.5
    c: DistanceX(g4,g-1) = 30
FEATURE [PartDesign::Pad] Pad012
  BaseFeature = -> AdditivePipe001
  Direction = (0,0,1)
  Length = 10
  Length2 = 10
  Profile = -> Sketch017
  ReferenceAxis = -> Sketch017 [N_Axis]
  Refine = true
  Suppressed = false
  Type = 3
  UpToFace = -> AdditivePipe001 [Face2]
FEATURE [PartDesign::LinearPattern] LinearPattern004
  BaseFeature = -> Pad012
  Direction = -> Sketch017 [H_Axis]
  Length = 60
  Mode = 0
  Occurrences = 5
  Offset = 15
  Originals = -> [Pad012]
  Refine = true
  Suppressed = false
  TransformMode = 0
FEATURE [Sketcher::SketchObject] Sketch018
  ArcFitTolerance = 1e-06
  AttachmentSupport = -> [XY_Plane004]
  ExternalGeometry = -> [LinearPattern004]
  FullyConstrained = true
  MakeInternals = false
  MapMode = 5
  sketch-geometry (5):
    g0: LineSegment StartX=42.5 StartY=29.25 StartZ=0 EndX=42.5 EndY=30.75 EndZ=0
    g1: LineSegment StartX=42.5 StartY=30.75 StartZ=0 EndX=-42.5 EndY=30.75 EndZ=0
    g2: LineSegment StartX=-42.5 StartY=30.75 StartZ=0 EndX=-42.5 EndY=29.25 EndZ=0
    g3: LineSegment StartX=-42.5 StartY=29.25 StartZ=0 EndX=42.5 EndY=29.25 EndZ=0
    g4: GeomPoint [constr] X=0 Y=30 Z=0
  constraints (13):
    c: Coincident(g0,g1)
    c: Coincident(g1,g2)
    c: Coincident(g2,g3)
    c: Coincident(g3,g0)
    c: Vertical(g0)
    c: Vertical(g2)
    c: Horizontal(g1)
    c: Horizontal(g3)
    c: Symmetric(g2,g0,g4)
    c: PointOnObject(g4,g-2)
    c: PointOnObject(g1,g-3)
    c: DistanceY(g4) = 30
    c: DistanceY(g0,g0) = 1.5
FEATURE [PartDesign::Pad] Pad013
  BaseFeature = -> LinearPattern004
  Direction = (0,0,1)
  Length = 10
  Length2 = 10
  Profile = -> Sketch018
  ReferenceAxis = -> Sketch018 [N_Axis]
  Refine = true
  Suppressed = false
  Type = 3
  UpToFace = -> LinearPattern004 [Face31]
FEATURE [PartDesign::LinearPattern] LinearPattern005
  BaseFeature = -> Pad013
  Direction = -> Sketch018 [V_Axis]
  Length = 60
  Mode = 0
  Occurrences = 5
  Offset = 15
  Originals = -> [Pad013]
  Refine = true
  Reversed = true
  Suppressed = false
  TransformMode = 0
FEATURE [PartDesign::CoordinateSystem] FanMountHole001
  AttacherType = Attacher::AttachEngine3D
  AttachmentSupport = -> [LinearPattern005]
  MapMode = 11
  Placement = pos=(-35.75,-35.75,0) rot=(0,0,1;1.5708rad)
FEATURE [Sketcher::SketchObject] Sketch019
  ArcFitTolerance = 1e-06
  AttachmentSupport = -> [XZ_Plane004]
  ExternalGeometry = -> [LinearPattern005]
  FullyConstrained = true
  MakeInternals = false
  MapMode = 5
  Placement = pos=(0,0,0) rot=(1,0,0;1.5708rad)
  sketch-geometry (4):
    g0: LineSegment StartX=60 StartY=14.5 StartZ=0 EndX=60 EndY=0 EndZ=0
    g1: LineSegment StartX=60 StartY=0 StartZ=0 EndX=43 EndY=0 EndZ=0
    g2: LineSegment StartX=43 StartY=0 StartZ=0 EndX=40.4433 EndY=14.5 EndZ=0
    g3: LineSegment StartX=40.4433 StartY=14.5 StartZ=0 EndX=60 EndY=14.5 EndZ=0
  constraints (11):
    c: Coincident(g-3,g0)
    c: PointOnObject(g0,g-1)
    c: Vertical(g0)
    c: Coincident(g0,g1)
    c: PointOnObject(g1,g-1)
    c: Coincident(g1,g2)
    c: PointOnObject(g2,g-3)
    c: Coincident(g2,g3)
    c: Coincident(g3,g0)
    c: DistanceX(g-1,g1) = 43
    c: Angle(g1,g2) = 1.74533
FEATURE [PartDesign::Pocket] Pocket002
  BaseFeature = -> LinearPattern005
  Direction = (0,1,-2e-16)
  Length = 5
  Length2 = 5
  Midplane = true
  Profile = -> Sketch019
  ReferenceAxis = -> Sketch019 [N_Axis]
  Refine = true
  Suppressed = false
  Type = 1
FEATURE [PartDesign::CoordinateSystem] FilterHolderMount001
  AttacherType = Attacher::AttachEngine3D
  AttachmentSupport = -> [Pocket002]
  MapMode = 11
  Placement = pos=(-35.75,35.75,1.5) rot=(0,0,1;1.5708rad)
FEATURE [PartDesign::CoordinateSystem] OtherFanHolder001
  AttacherType = Attacher::AttachEngine3D
  AttachmentSupport = -> [Pocket002]
  MapMode = 45
  Placement = pos=(42.8701,0,0.736527) rot=(0.642788,0,0.766044;3.14159rad)
FEATURE [Sketcher::SketchObject] Sketch022
  ArcFitTolerance = 1e-06
  FullyConstrained = true
  MakeInternals = false
  MapMode = 5
  Placement = pos=(41.7034,1.6e-15,7.35343) rot=(0.540716,0.540716,0.6444;1.99673rad)
  sketch-geometry (6):
    g0: ArcOfCircle CenterX=43.0908 CenterY=-0.761797 CenterZ=0 NormalX=0 NormalY=0 NormalZ=1 AngleXU=0 Radius=0.6 StartAngle=2.49691 EndAngle=3.31716
    g1: LineSegment StartX=44.66 StartY=3.6334 StartZ=0 EndX=42.6112 EndY=-0.401229 EndZ=0
    g2: LineSegment StartX=42.5 StartY=-5.3666 StartZ=0 EndX=42.5 EndY=-0.866599 EndZ=0
    g3: LineSegment StartX=42.5 StartY=-5.3666 StartZ=0 EndX=50.5 EndY=-5.3666 EndZ=0
    g4: LineSegment StartX=44.66 StartY=3.6334 StartZ=0 EndX=50.5 EndY=3.6334 EndZ=0
    g5: ArcOfCircle CenterX=50.5 CenterY=-0.866599 CenterZ=0 NormalX=0 NormalY=0 NormalZ=1 AngleXU=0 Radius=4.5 StartAngle=4.71239 EndAngle=7.85398
  constraints (16):
    c: Coincident(g0,g-3)
    c: Coincident(g0,g-4)
    c: Radius(g0) = 0.6
    c: Coincident(g3,g2)
    c: Horizontal(g3)
    c: Coincident(g4,g1)
    c: Horizontal(g4)
    c: Diameter(g5) = 9
    c: PointOnObject(g1,g-4)
    c: Horizontal(g5,g2)
    c: Tangent(g5,g3) = -1.5708
    c: Tangent(g5,g4) = 1.5708
    c: DistanceX(g-4,g5) = 4
    c: Coincident(g2,g0)
    c: Coincident(g0,g1)
    c: PointOnObject(g2,g-3)
FEATURE [PartDesign::Pocket] Pocket003
  BaseFeature = -> Pocket002
  Direction = (-0.984808,2e-16,-0.173648)
  Length = 50
  Length2 = 5
  Midplane = true
  Profile = -> Sketch022
  ReferenceAxis = -> Sketch022 [N_Axis]
  Refine = true
  Suppressed = false
  Type = 0
FEATURE [PartDesign::Body] Body003  label="Fan2Holder"
  AllowCompound = false
  Group = -> [Sketch014,Pad010,Sketch015,Pad011,Sketch016,AdditivePipe001,Sketch017,Pad012,LinearPattern004,Sketch018,Pad013,LinearPattern005,FanMountHole001,Sketch019,Pocket002,OtherFanHolder001,FilterHolderMount001,Sketch022,Pocket003]
  Origin = -> Origin004
  Tip = -> Pocket003
FEATURE [Sketcher::SketchObject] Sketch023
  ArcFitTolerance = 1e-06
  AttachmentSupport = -> [XY_Plane003]
  FullyConstrained = true
  MakeInternals = false
  MapMode = 5
  sketch-geometry (10):
    g0: LineSegment StartX=-55 StartY=25 StartZ=0 EndX=-55 EndY=-25 EndZ=0
    g1: LineSegment StartX=-45 StartY=-35 StartZ=0 EndX=45 EndY=-35 EndZ=0
    g2: LineSegment StartX=55 StartY=-25 StartZ=0 EndX=55 EndY=25 EndZ=0
    g3: LineSegment StartX=45 StartY=35 StartZ=0 EndX=-45 EndY=35 EndZ=0
    g4: ArcOfCircle CenterX=-45 CenterY=25 CenterZ=0 NormalX=0 NormalY=0 NormalZ=1 AngleXU=0 Radius=10 StartAngle=1.5708 EndAngle=3.14159
    g5: ArcOfCircle CenterX=-45 CenterY=-25 CenterZ=0 NormalX=0 NormalY=0 NormalZ=1 AngleXU=0 Radius=10 StartAngle=3.14159 EndAngle=4.71239
    g6: ArcOfCircle CenterX=45 CenterY=-25 CenterZ=0 NormalX=0 NormalY=0 NormalZ=1 AngleXU=0 Radius=10 StartAngle=4.71239 EndAngle=6.28319
    g7: ArcOfCircle CenterX=45 CenterY=25 CenterZ=0 NormalX=0 NormalY=0 NormalZ=1 AngleXU=0 Radius=10 StartAngle=1e-16 EndAngle=1.5708
    g8: GeomPoint [constr] X=-55 Y=35 Z=0
    g9: GeomPoint [constr] X=55 Y=-35 Z=0
  constraints (22):
    c: Tangent(g0,g4) = -1.5708
    c: Tangent(g0,g5) = -1.5708
    c: Tangent(g1,g5) = -1.5708
    c: Tangent(g1,g6) = -1.5708
    c: Tangent(g2,g6) = -1.5708
    c: Tangent(g2,g7) = -1.5708
    c: Tangent(g3,g7) = -1.5708
    c: Tangent(g3,g4) = -1.5708
    c: Vertical(g2)
    c: Horizontal(g1)
    c: Equal(g4,g5)
    c: Equal(g5,g6)
    c: Equal(g6,g7)
    c: PointOnObject(g8,g0)
    c: PointOnObject(g8,g3)
    c: PointOnObject(g9,g1)
    c: PointOnObject(g9,g2)
    c: Symmetric(g3,g3,g-2)
    c: Symmetric(g0,g0,g-1)
    c: DistanceX(g0,g2) = 110
    c: DistanceY(g1,g3) = 70
    c: Radius(g7) = 10
FEATURE [PartDesign::Pad] Pad014
  Direction = (0,0,1)
  Length = 20
  Length2 = 10
  Profile = -> Sketch023
  ReferenceAxis = -> Sketch023 [N_Axis]
  Refine = true
  Suppressed = false
  Type = 0
FEATURE [Sketcher::SketchObject] Sketch024
  ArcFitTolerance = 1e-06
  AttachmentSupport = -> [XZ_Plane003]
  ExternalGeometry = -> [Pad014]
  FullyConstrained = true
  MakeInternals = false
  MapMode = 5
  Placement = pos=(0,0,0) rot=(1,0,0;1.5708rad)
  sketch-geometry (5):
    g0: LineSegment StartX=55 StartY=20 StartZ=0 EndX=45 EndY=20 EndZ=0
    g1: ArcOfCircle CenterX=45 CenterY=16 CenterZ=0 NormalX=0 NormalY=0 NormalZ=1 AngleXU=0 Radius=4 StartAngle=0.413862 EndAngle=1.5708
    g2: ArcOfCircle CenterX=47 CenterY=1.5 CenterZ=0 NormalX=0 NormalY=0 NormalZ=1 AngleXU=0 Radius=8 StartAngle=3e-16 EndAngle=0.413862
    g3: LineSegment StartX=54.3246 StartY=4.71719 StartZ=0 EndX=48.6623 EndY=17.6086 EndZ=0
    g4: LineSegment StartX=55 StartY=20 StartZ=0 EndX=55 EndY=1.5 EndZ=0
  constraints (12):
    c: Horizontal(g0)
    c: Tangent(g1,g0) = -1.5708
    c: Tangent(g3,g2) = -1.5708
    c: Tangent(g3,g1) = -1.5708
    c: Coincident(g0,g-3)
    c: Coincident(g4,g0)
    c: PointOnObject(g4,g-3)
    c: Tangent(g4,g2) = 1.5708
    c: DistanceY(g2) = 1.5
    c: DistanceX(g0,g0) = 10
    c: Radius(g2) = 8
    c: Radius(g1) = 4
FEATURE [PartDesign::SubtractivePipe] SubtractivePipe
  AuxilleryCurvelinear = true
  AuxillerySpineTangent = false
  BaseFeature = -> Pad014
  Binormal = (0,0,0)
  Mode = 0
  Profile = -> Sketch024
  Refine = true
  Spine = -> Pad014 [Edge16,Edge19,Edge22,Edge24,Edge4,Edge7,Edge10,Edge13]
  SpineTangent = false
  Suppressed = false
  Transformation = 0
  Transition = 0
FEATURE [Sketcher::SketchObject] Sketch025
  ArcFitTolerance = 1e-06
  AttachmentSupport = -> [YZ_Plane003]
  ExternalGeometry = -> [SubtractivePipe]
  FullyConstrained = true
  MakeInternals = false
  MapMode = 5
  Placement = pos=(0,0,0) rot=(0.57735,0.57735,0.57735;2.0944rad)
  sketch-geometry (7):
    g0: LineSegment StartX=-7.5 StartY=20 StartZ=0 EndX=7.5 EndY=20 EndZ=0
    g1: ArcOfCircle CenterX=7.5 CenterY=23 CenterZ=0 NormalX=0 NormalY=0 NormalZ=1 AngleXU=0 Radius=3 StartAngle=3.14159 EndAngle=4.71239
    g2: ArcOfCircle CenterX=-7.5 CenterY=23 CenterZ=0 NormalX=0 NormalY=0 NormalZ=1 AngleXU=0 Radius=3 StartAngle=4.71239 EndAngle=6.28319
    g3: ArcOfCircle CenterX=8.84e-14 CenterY=28 CenterZ=0 NormalX=0 NormalY=0 NormalZ=1 AngleXU=0 Radius=4.5 StartAngle=-6.7475e-12 EndAngle=3.14159
    g4: LineSegment StartX=4.5 StartY=23 StartZ=0 EndX=4.5 EndY=28 EndZ=0
    g5: LineSegment StartX=-4.5 StartY=23 StartZ=0 EndX=-4.5 EndY=28 EndZ=0
    g6: Circle CenterX=8.84e-14 CenterY=28 CenterZ=0 NormalX=0 NormalY=0 NormalZ=1 AngleXU=0 Radius=2.75
  constraints (16):
    c: PointOnObject(g0,g-3)
    c: Symmetric(g0,g0,g-2)
    c: Vertical(g5)
    c: Tangent(g4,g3) = -1.5708
    c: Tangent(g4,g1) = 1.5708
    c: Tangent(g1,g0) = -1.5708
    c: Tangent(g2,g0) = -1.5708
    c: Tangent(g5,g2) = -1.5708
    c: Tangent(g5,g3) = 1.5708
    c: Vertical(g4)
    c: Equal(g1,g2)
    c: Diameter(g3) = 9
    c: Coincident(g6,g3)
    c: Diameter(g6) = 5.5
    c: Radius(g1) = 3
    c: DistanceY(g0,g3) = 8
FEATURE [PartDesign::Pad] Pad015
  BaseFeature = -> SubtractivePipe
  Direction = (1,0,0)
  Length = 70
  Length2 = 10
  Midplane = true
  Profile = -> Sketch025
  ReferenceAxis = -> Sketch025 [N_Axis]
  Refine = true
  Suppressed = false
  Type = 0
FEATURE [Sketcher::SketchObject] Sketch026
  ArcFitTolerance = 1e-06
  AttachmentSupport = -> [XZ_Plane003]
  ExternalGeometry = -> [Pad015]
  FullyConstrained = true
  MakeInternals = false
  MapMode = 5
  Placement = pos=(0,0,0) rot=(1,0,0;1.5708rad)
  sketch-geometry (5):
    g0: LineSegment StartX=-25.5 StartY=35 StartZ=0 EndX=-25.5 EndY=20 EndZ=0
    g1: LineSegment StartX=-25.5 StartY=20 StartZ=0 EndX=25.5 EndY=20 EndZ=0
    g2: LineSegment StartX=25.5 StartY=20 StartZ=0 EndX=25.5 EndY=35 EndZ=0
    g3: LineSegment StartX=25.5 StartY=35 StartZ=0 EndX=-25.5 EndY=35 EndZ=0
    g4: GeomPoint [constr] X=0 Y=27.5 Z=0
  constraints (13):
    c: Coincident(g0,g1)
    c: Coincident(g1,g2)
    c: Coincident(g2,g3)
    c: Coincident(g3,g0)
    c: Vertical(g0)
    c: Vertical(g2)
    c: Horizontal(g1)
    c: Horizontal(g3)
    c: Symmetric(g2,g0,g4)
    c: PointOnObject(g4,g-2)
    c: PointOnObject(g1,g-3)
    c: DistanceX(g3,g3) = 51
    c: DistanceY(g2,g2) = 15
FEATURE [PartDesign::Pocket] Pocket004
  BaseFeature = -> Pad015
  Direction = (0,1,-2e-16)
  Length = 5
  Length2 = 5
  Midplane = true
  Profile = -> Sketch026
  ReferenceAxis = -> Sketch026 [N_Axis]
  Refine = true
  Suppressed = false
  Type = 1
FEATURE [Sketcher::SketchObject] Sketch027
  ArcFitTolerance = 1e-06
  AttachmentSupport = -> [Pocket004]
  ExternalGeometry = -> [Pocket004]
  FullyConstrained = true
  MakeInternals = false
  MapMode = 5
  Placement = pos=(0,-30.5104,13.4011) rot=(1,0,0;1.15693rad)
  sketch-geometry (5):
    g0: LineSegment StartX=-34.25 StartY=0 StartZ=0 EndX=-34.25 EndY=-4 EndZ=0
    g1: LineSegment StartX=-34.25 StartY=-4 StartZ=0 EndX=-26.25 EndY=-4 EndZ=0
    g2: LineSegment StartX=-26.25 StartY=-4 StartZ=0 EndX=-26.25 EndY=0 EndZ=0
    g3: LineSegment StartX=-26.25 StartY=0 StartZ=0 EndX=-34.25 EndY=0 EndZ=0
    g4: LineSegment [constr] StartX=-30.25 StartY=0 StartZ=0 EndX=-30.25 EndY=15.2954 EndZ=0
  constraints (14):
    c: Coincident(g0,g1)
    c: Coincident(g1,g2)
    c: Coincident(g2,g3)
    c: Coincident(g3,g0)
    c: Vertical(g0)
    c: Vertical(g2)
    c: Horizontal(g1)
    c: Horizontal(g3)
    c: PointOnObject(g0,g-1)
    c: DistanceY(g2,g2) = 4
    c: DistanceX(g1,g1) = 8
    c: Symmetric(g3,g3,g4)
    c: Vertical(g4)
    c: Symmetric(g-3,g-3,g4)
FEATURE [PartDesign::Pocket] Pocket005
  BaseFeature = -> Pocket004
  Direction = (0,0.915575,-0.402148)
  Length = 10
  Length2 = 5
  Profile = -> Sketch027
  ReferenceAxis = -> Sketch027 [N_Axis]
  Refine = true
  Suppressed = false
  Type = 0
FEATURE [Sketcher::SketchObject] Sketch028
  ArcFitTolerance = 1e-06
  AttachmentSupport = -> [Pocket005]
  ExternalGeometry = -> [Pocket005]
  FullyConstrained = true
  MakeInternals = false
  MapMode = 5
  Placement = pos=(-2.8e-15,35,0) rot=(0,0.707107,0.707107;3.14159rad)
  sketch-geometry (6):
    g0: LineSegment StartX=24.25 StartY=15.1629 StartZ=0 EndX=24.25 EndY=7.16289 EndZ=0
    g1: LineSegment StartX=24.25 StartY=7.16289 StartZ=0 EndX=36.25 EndY=7.16289 EndZ=0
    g2: LineSegment StartX=36.25 StartY=7.16289 StartZ=0 EndX=36.25 EndY=15.1629 EndZ=0
    g3: LineSegment StartX=36.25 StartY=15.1629 StartZ=0 EndX=24.25 EndY=15.1629 EndZ=0
    g4: LineSegment [constr] StartX=30.25 StartY=15.1629 StartZ=0 EndX=30.25 EndY=23 EndZ=0
    g5: LineSegment [constr] StartX=45 StartY=11.1629 StartZ=0 EndX=36.25 EndY=11.1629 EndZ=0
  constraints (16):
    c: Coincident(g0,g1)
    c: Coincident(g1,g2)
    c: Coincident(g2,g3)
    c: Coincident(g3,g0)
    c: Vertical(g0)
    c: Vertical(g2)
    c: Horizontal(g1)
    c: Horizontal(g3)
    c: Symmetric(g3,g3,g4)
    c: Symmetric(g-3,g-3,g4)
    c: Vertical(g4)
    c: DistanceX(g3,g3) = 12
    c: DistanceY(g2,g2) = 8
    c: Symmetric(g-4,g-4,g5)
    c: Symmetric(g2,g2,g5)
    c: Horizontal(g5)
FEATURE [PartDesign::Pocket] Pocket006
  BaseFeature = -> Pocket005
  Direction = (0,-1,2e-16)
  Length = 63
  Length2 = 5
  Profile = -> Sketch028
  ReferenceAxis = -> Sketch028 [N_Axis]
  Refine = true
  Suppressed = false
  Type = 0
FEATURE [Sketcher::SketchObject] Sketch029
  ArcFitTolerance = 1e-06
  AttachmentSupport = -> [Pocket006]
  ExternalGeometry = -> [Pocket006]
  FullyConstrained = true
  MakeInternals = false
  MapMode = 5
  Placement = pos=(0,0,0) rot=(1,0,0;3.14159rad)
  sketch-geometry (10):
    g0: LineSegment StartX=-45 StartY=20 StartZ=0 EndX=-45 EndY=-20 EndZ=0
    g1: LineSegment StartX=-40 StartY=-25 StartZ=0 EndX=40 EndY=-25 EndZ=0
    g2: LineSegment StartX=45 StartY=-20 StartZ=0 EndX=45 EndY=20 EndZ=0
    g3: LineSegment StartX=40 StartY=25 StartZ=0 EndX=-40 EndY=25 EndZ=0
    g4: ArcOfCircle CenterX=-40 CenterY=20 CenterZ=0 NormalX=0 NormalY=0 NormalZ=1 AngleXU=0 Radius=5 StartAngle=1.5708 EndAngle=3.14159
    g5: ArcOfCircle CenterX=-40 CenterY=-20 CenterZ=0 NormalX=0 NormalY=0 NormalZ=1 AngleXU=0 Radius=5 StartAngle=3.14159 EndAngle=4.71239
    g6: ArcOfCircle CenterX=40 CenterY=-20 CenterZ=0 NormalX=0 NormalY=0 NormalZ=1 AngleXU=0 Radius=5 StartAngle=4.71239 EndAngle=6.28319
    g7: ArcOfCircle CenterX=40 CenterY=20 CenterZ=0 NormalX=0 NormalY=0 NormalZ=1 AngleXU=0 Radius=5 StartAngle=9.685e-13 EndAngle=1.5708
    g8: GeomPoint [constr] X=-45 Y=25 Z=0
    g9: GeomPoint [constr] X=45 Y=-25 Z=0
  constraints (22):
    c: Tangent(g0,g4) = -1.5708
    c: Tangent(g0,g5) = -1.5708
    c: Tangent(g1,g5) = -1.5708
    c: Tangent(g1,g6) = -1.5708
    c: Tangent(g2,g6) = -1.5708
    c: Tangent(g2,g7) = -1.5708
    c: Tangent(g3,g7) = -1.5708
    c: Tangent(g3,g4) = -1.5708
    c: Vertical(g2)
    c: Horizontal(g1)
    c: Equal(g4,g5)
    c: Equal(g5,g6)
    c: Equal(g6,g7)
    c: PointOnObject(g8,g0)
    c: PointOnObject(g8,g3)
    c: PointOnObject(g9,g1)
    c: PointOnObject(g9,g2)
    c: Radius(g5) = 5
    c: Symmetric(g3,g3,g-2)
    c: Symmetric(g0,g0,g-1)
    c: DistanceX(g2,g-3) = 10
    c: DistanceY(g3,g-4) = 10
FEATURE [PartDesign::Pocket] Pocket007
  BaseFeature = -> Pocket006
  Direction = (0,0,1)
  Length = 15
  Length2 = 5
  Profile = -> Sketch029
  ReferenceAxis = -> Sketch029 [N_Axis]
  Refine = true
  Suppressed = false
  Type = 0
FEATURE [PartDesign::CoordinateSystem] Fan  label="FanHolders"
  AttacherType = Attacher::AttachEngine3D
  AttachmentSupport = -> [Pocket007]
  MapMode = 45
  Placement = pos=(0,1.014e-13,28) rot=(0.57735,0.57735,0.57735;2.0944rad)
FEATURE [PartDesign::CoordinateSystem] Bottom
  AttacherType = Attacher::AttachEngine3D
  AttachmentSupport = -> [Pocket007]
  MapMode = 45
  Placement = pos=(-2.3879e-12,-1.227e-13,0) rot=(0,0,1;1.5708rad)
FEATURE [PartDesign::Body] Body002  label="Base"
  AllowCompound = false
  Group = -> [Sketch023,Pad014,Sketch024,SubtractivePipe,Sketch025,Pad015,Sketch026,Pocket004,Sketch027,Pocket005,Sketch028,Pocket006,Sketch029,Pocket007,Fan,Bottom]
  Origin = -> Origin003
  Tip = -> Pocket007
FEATURE [Sketcher::SketchObject] Sketch030
  ArcFitTolerance = 1e-06
  AttachmentSupport = -> [XY_Plane005]
  FullyConstrained = true
  MakeInternals = false
  MapMode = 5
  sketch-geometry (10):
    g0: LineSegment StartX=-55 StartY=25 StartZ=0 EndX=-55 EndY=-25 EndZ=0
    g1: LineSegment StartX=-45 StartY=-35 StartZ=0 EndX=45 EndY=-35 EndZ=0
    g2: LineSegment StartX=55 StartY=-25 StartZ=0 EndX=55 EndY=25 EndZ=0
    g3: LineSegment StartX=45 StartY=35 StartZ=0 EndX=-45 EndY=35 EndZ=0
    g4: ArcOfCircle CenterX=-45 CenterY=25 CenterZ=0 NormalX=0 NormalY=0 NormalZ=1 AngleXU=0 Radius=10 StartAngle=1.5708 EndAngle=3.14159
    g5: ArcOfCircle CenterX=-45 CenterY=-25 CenterZ=0 NormalX=0 NormalY=0 NormalZ=1 AngleXU=0 Radius=10 StartAngle=3.14159 EndAngle=4.71239
    g6: ArcOfCircle CenterX=45 CenterY=-25 CenterZ=0 NormalX=0 NormalY=0 NormalZ=1 AngleXU=0 Radius=10 StartAngle=4.71239 EndAngle=6.28319
    g7: ArcOfCircle CenterX=45 CenterY=25 CenterZ=0 NormalX=0 NormalY=0 NormalZ=1 AngleXU=0 Radius=10 StartAngle=0 EndAngle=1.5708
    g8: GeomPoint [constr] X=-55 Y=35 Z=0
    g9: GeomPoint [constr] X=55 Y=-35 Z=0
  constraints (22):
    c: Tangent(g0,g4) = -1.5708
    c: Tangent(g0,g5) = -1.5708
    c: Tangent(g1,g5) = -1.5708
    c: Tangent(g1,g6) = -1.5708
    c: Tangent(g2,g6) = -1.5708
    c: Tangent(g2,g7) = -1.5708
    c: Tangent(g3,g7) = -1.5708
    c: Tangent(g3,g4) = -1.5708
    c: Vertical(g2)
    c: Horizontal(g1)
    c: Equal(g4,g5)
    c: Equal(g5,g6)
    c: Equal(g6,g7)
    c: PointOnObject(g8,g0)
    c: PointOnObject(g8,g3)
    c: PointOnObject(g9,g1)
    c: PointOnObject(g9,g2)
    c: Radius(g5) = 10
    c: Symmetric(g3,g3,g-2)
    c: Symmetric(g0,g0,g-1)
    c: DistanceX(g0,g2) = 110
    c: DistanceY(g1,g3) = 70
FEATURE [App::Link] Base  label="Base001"
  AttachedBy = #Bottom
  AttachedTo = Parent Assembly#LCS_Origin
  AttachmentOffset = pos=(0,0,0) rot=(0,0,1;1.5708rad)
  LinkPlacement = pos=(2.3879e-12,1.227e-13,0) rot=(0,0,1;0rad)
  LinkedObject = -> Body002
  Placement = pos=(2.3879e-12,1.227e-13,0) rot=(0,0,1;0rad)
  SolverId = Asm4EE
  expr: Placement = LCS_Origin.Placement * AttachmentOffset * Bottom.Placement ^ -1
FEATURE [App::Link] Fan1Holder  label="Fan1Holder001"
  AttachedBy = #Mount1
  AttachedTo = Base#Fan
  AttachmentOffset = pos=(0,0,0) rot=(0.707107,-0.707107,0;3.14159rad)
  LinkPlacement = pos=(2.3343e-12,6.5,78.5) rot=(-0.57735,0.57735,-0.57735;4.18879rad)
  LinkedObject = -> Body
  Placement = pos=(2.3343e-12,6.5,78.5) rot=(-0.57735,0.57735,-0.57735;4.18879rad)
  SolverId = Asm4EE
  expr: Placement = Base.Placement * Fan.Placement * AttachmentOffset * Mount1.Placement ^ -1
FEATURE [App::Link] Fan2Holder  label="Fan2Holder001"
  AttachedBy = #OtherFanHolder001
  AttachedTo = Fan1Holder#OtherFanHolder
  AttachmentOffset = pos=(0,0,0) rot=(1,0,0;3.14159rad)
  LinkPlacement = pos=(2.45e-12,-8.20687,161.907) rot=(0.633687,0.633687,-0.443713;2.30637rad)
  LinkedObject = -> Body003
  Placement = pos=(2.45e-12,-8.20687,161.907) rot=(0.633687,0.633687,-0.443713;2.30637rad)
  SolverId = Asm4EE
  expr: Placement = Fan1Holder.Placement * OtherFanHolder.Placement * AttachmentOffset * OtherFanHolder001.Placement ^ -1
FEATURE [App::Link] FilterHolder  label="FilterHolder001"
  AttachedBy = #FanHolder
  AttachedTo = Fan1Holder#FilterHolderMount
  AttachmentOffset = pos=(0,0,0) rot=(-0.707107,-0.707107,0;3.14159rad)
  LinkPlacement = pos=(2.3874e-12,0.5,78.5) rot=(-1,0,0;1.5708rad)
  LinkedObject = -> Body001
  Placement = pos=(2.3874e-12,0.5,78.5) rot=(-1,0,0;1.5708rad)
  SolverId = Asm4EE
  expr: Placement = Fan1Holder.Placement * FilterHolderMount.Placement * AttachmentOffset * FanHolder.Placement ^ -1
FEATURE [App::Link] FilterHolder001  label="FilterHolder002"
  AttachedBy = #FanHolder
  AttachedTo = Fan2Holder#FilterHolderMount001
  AttachmentOffset = pos=(0,0,0) rot=(-0.707107,-0.707107,0;3.14159rad)
  LinkPlacement = pos=(2.494e-12,-13.845,159.855) rot=(0,-0.573576,-0.819152;3.14159rad)
  LinkedObject = -> Body001
  Placement = pos=(2.494e-12,-13.845,159.855) rot=(0,-0.573576,-0.819152;3.14159rad)
  SolverId = Asm4EE
  expr: Placement = Fan2Holder.Placement * FilterHolderMount001.Placement * AttachmentOffset * FanHolder.Placement ^ -1
FEATURE [App::Link] _0mmAxialFan  label="80mmAxialFan"
  AttachedBy = #FanHouse_TopMountHole
  AttachedTo = Fan1Holder#FanMountHole
  AttachmentOffset = pos=(0,0,0) rot=(0,0,1;1.5708rad)
  LinkPlacement = pos=(2.1458e-12,31.5,78.5) rot=(0,0.707107,-0.707107;3.14159rad)
  LinkedObject = -> <external Axial Fan.FCStd>#Assembly
  Placement = pos=(2.1458e-12,31.5,78.5) rot=(0,0.707107,-0.707107;3.14159rad)
  SolverId = Asm4EE
  expr: Placement = Fan1Holder.Placement * FanMountHole.Placement * AttachmentOffset * Axial_Fan#FanHouse_TopMountHole.Placement ^ -1
FEATURE [App::Link] _0mmAxialFan001  label="80mmAxialFan001"
  AttachedBy = #FanHouse_TopMountHole
  AttachedTo = Fan2Holder#FanMountHole001
  AttachmentOffset = pos=(0,0,0) rot=(0,0,1;1.5708rad)
  LinkPlacement = pos=(2.2666e-12,15.2854,170.457) rot=(1,0,0;1.91986rad)
  LinkedObject = -> <external Axial Fan.FCStd>#Assembly
  Placement = pos=(2.2666e-12,15.2854,170.457) rot=(1,0,0;1.91986rad)
  SolverId = Asm4EE
  expr: Placement = Fan2Holder.Placement * FanMountHole001.Placement * AttachmentOffset * Axial_Fan#FanHouse_TopMountHole.Placement ^ -1
FEATURE [App::Link] BottomCover  label="BottomCover001"
  AttachedBy = #Base001
  AttachedTo = Base#Bottom
  LinkPlacement = pos=(8.91e-14,6.93e-14,-1.5) rot=(0,0,1;0rad)
  LinkedObject = -> Body004
  Placement = pos=(8.91e-14,6.93e-14,-1.5) rot=(0,0,1;0rad)
  SolverId = Asm4EE
  expr: Placement = Base.Placement * Bottom.Placement * AttachmentOffset * Base001.Placement ^ -1
FEATURE [PartDesign::Pad] Pad016
  Direction = (0,0,1)
  Length = 1.5
  Length2 = 10
  Profile = -> Sketch030
  ReferenceAxis = -> Sketch030 [N_Axis]
  Refine = true
  Suppressed = false
  Type = 0
FEATURE [PartDesign::CoordinateSystem] Base001  label="Base002"
  AttacherType = Attacher::AttachEngine3D
  AttachmentSupport = -> [Pad016]
  MapMode = 45
  Placement = pos=(-8.91e-14,-6.93e-14,1.5) rot=(0,0,1;1.5708rad)
FEATURE [PartDesign::Body] Body004  label="BottomCover"
  AllowCompound = false
  Group = -> [Sketch030,Base001,Pad016]
  Origin = -> Origin005
  Tip = -> Pad016
FEATURE [App::Link] Base002  label="Base003"
  AttachedBy = #Fan
  AttachedTo = Fan1Holder#Mount2
  AttachmentOffset = pos=(0,0,0) rot=(0,0,1;4.71239rad)
  LinkPlacement = pos=(50.5,27.5746,125.216) rot=(0.60812,-0.60812,0.510274;2.19793rad)
  LinkedObject = -> Body002
  Placement = pos=(50.5,27.5746,125.216) rot=(0.60812,-0.60812,0.510274;2.19793rad)
  SolverId = Asm4EE
  expr: Placement = Fan1Holder.Placement * Mount2.Placement * AttachmentOffset * Fan.Placement ^ -1
FEATURE [App::Link] BottomCover001  label="BottomCover002"
  AttachedBy = #Base001
  AttachedTo = Base002#Bottom
  LinkPlacement = pos=(50.5,29.0518,125.476) rot=(0.60812,-0.60812,0.510274;2.19793rad)
  LinkedObject = -> Body004
  Placement = pos=(50.5,29.0518,125.476) rot=(0.60812,-0.60812,0.510274;2.19793rad)
  SolverId = Asm4EE
  expr: Placement = Base002.Placement * Bottom.Placement * AttachmentOffset * Base001.Placement ^ -1
FEATURE [App::Part] Assembly
  AssemblyType = Part::Link
  Group = -> [LCS_Origin,Constraints,Variables,Configurations,Base,Fan1Holder,Fan2Holder,FilterHolder,FilterHolder001,_0mmAxialFan,_0mmAxialFan001,BottomCover,Base002,BottomCover001]
  Origin = -> Origin001
  Type = Assembly
FEATURE [Sketcher::SketchObject] Sketch031
  ArcFitTolerance = 1e-06
  AttachmentSupport = -> [XZ_Plane]
  FullyConstrained = true
  MakeInternals = false
  MapMode = 5
  Placement = pos=(0,0,0) rot=(1,0,0;1.5708rad)
  sketch-geometry (8):
    g0: LineSegment StartX=0 StartY=0 StartZ=0 EndX=0 EndY=-5 EndZ=0
    g1: LineSegment StartX=0 StartY=-5 StartZ=0 EndX=43 EndY=-5 EndZ=0
    g2: LineSegment StartX=43 StartY=-5 StartZ=0 EndX=43 EndY=1.24e-14 EndZ=0
    g3: LineSegment StartX=43 StartY=1.24e-14 StartZ=0 EndX=0 EndY=0 EndZ=0
    g4: LineSegment StartX=43 StartY=1.24e-14 StartZ=0 EndX=44.7101 EndY=-4.69846 EndZ=0
    g5: LineSegment StartX=44.7101 StartY=-4.69846 StartZ=0 EndX=85.1169 EndY=10.0084 EndZ=0
    g6: LineSegment StartX=85.1169 StartY=10.0084 StartZ=0 EndX=83.4068 EndY=14.7069 EndZ=0
    g7: LineSegment StartX=83.4068 StartY=14.7069 StartZ=0 EndX=43 EndY=1.24e-14 EndZ=0
  constraints (22):
    c: Angle(g-3,g-1) = 1.39626
    c: Coincident(g0,g1)
    c: Coincident(g1,g2)
    c: Coincident(g2,g3)
    c: Coincident(g3,g0)
    c: Vertical(g0)
    c: Vertical(g2)
    c: Horizontal(g1)
    c: Coincident(g0,g-1)
    c: Coincident(g2,g-3)
    c: DistanceY(g2,g2) = 5
    c: Coincident(g2,g4)
    c: Coincident(g4,g5)
    c: Coincident(g5,g6)
    c: Coincident(g6,g7)
    c: Coincident(g7,g4)
    c: Perpendicular(g7,g4)
    c: Perpendicular(g6,g7)
    c: Equal(g4,g6)
    c: Equal(g6,g2)
    c: Equal(g7,g1)
    c: Angle(g7,g-3) = 1.39626
FEATURE [PartDesign::Pocket] Pocket008
  BaseFeature = -> Pad009
  Direction = (0,1,-2e-16)
  Length = 5
  Length2 = 5
  Profile = -> Sketch031
  ReferenceAxis = -> Sketch031 [N_Axis]
  Refine = true
  Reversed = true
  Suppressed = false
  Type = 1
FEATURE [PartDesign::CoordinateSystem] Mount1
  AttacherType = Attacher::AttachEngine3D
  AttachmentSupport = -> [Pocket008]
  MapMode = 45
  Placement = pos=(-50.5,-7e-16,6.5) rot=(0,0.707107,0.707107;3.14159rad)
FEATURE [PartDesign::CoordinateSystem] Mount2
  AttacherType = Attacher::AttachEngine3D
  AttachmentOffset = pos=(0,0,25) rot=(0,0,1;0rad)
  AttachmentSupport = -> [Pocket008]
  MapMode = 11
  Placement = pos=(41.8539,-50.5,6.5) rot=(0.642788,0,0.766044;3.14159rad)
FEATURE [Sketcher::SketchObject] Sketch032
  ArcFitTolerance = 1e-06
  AttachmentSupport = -> [XZ_Plane]
  ExternalGeometry = -> [Pocket008]
  FullyConstrained = true
  MakeInternals = false
  MapMode = 5
  Placement = pos=(0,0,0) rot=(1,0,0;1.5708rad)
  sketch-geometry (7):
    g0: LineSegment StartX=41.2355 StartY=1.5 StartZ=0 EndX=42.7355 EndY=1.5 EndZ=0
    g1: LineSegment StartX=42.7355 StartY=1.5 StartZ=0 EndX=44.145 EndY=2.01303 EndZ=0
    g2: ArcOfCircle CenterX=41.2355 CenterY=2.10733 CenterZ=0 NormalX=0 NormalY=0 NormalZ=1 AngleXU=0 Radius=0.607328 StartAngle=4.71239 EndAngle=6.06406
    g3: ArcOfCircle CenterX=43.9373 CenterY=2.58373 CenterZ=0 NormalX=0 NormalY=0 NormalZ=1 AngleXU=0 Radius=0.607328 StartAngle=3.70978 EndAngle=5.06145
    g4: LineSegment StartX=42.3157 StartY=2.4414 StartZ=0 EndX=42.8081 EndY=2.52822 EndZ=0
    g5: ArcOfCircle CenterX=42.4211 CenterY=1.84329 CenterZ=0 NormalX=0 NormalY=0 NormalZ=1 AngleXU=0 Radius=0.607328 StartAngle=1.74533 EndAngle=2.92247
    g6: ArcOfCircle CenterX=42.9135 CenterY=1.93012 CenterZ=0 NormalX=0 NormalY=0 NormalZ=1 AngleXU=0 Radius=0.607328 StartAngle=0.568188 EndAngle=1.74533
  constraints (17):
    c: Coincident(g0,g-4)
    c: Horizontal(g0)
    c: Coincident(g0,g1)
    c: DistanceX(g0,g0) = 1.5
    c: Angle(g1,g-4) = 1.39626
    c: Symmetric(g4,g4,g-4)
    c: Tangent(g5,g4) = 1.5708
    c: Tangent(g5,g2) = 1.5708
    c: Tangent(g6,g4) = 1.5708
    c: Tangent(g6,g3) = 1.5708
    c: Tangent(g3,g1) = -1.5708
    c: Tangent(g2,g0) = -1.5708
    c: Equal(g2,g5)
    c: Equal(g5,g6)
    c: Equal(g6,g3)
    c: Distance(g0,g4) = 1
    c: Distance(g4) = 0.5
FEATURE [PartDesign::AdditivePipe] AdditivePipe002
  AuxilleryCurvelinear = true
  AuxillerySpineTangent = false
  BaseFeature = -> Pocket008
  Binormal = (0,0,0)
  Mode = 0
  Profile = -> Sketch032
  Refine = true
  Spine = -> Pocket008 [Edge9,Edge146,Edge145,Edge144,Edge2,Edge147,Edge148]
  SpineTangent = false
  Suppressed = false
  Transformation = 0
  Transition = 1
FEATURE [PartDesign::Body] Body  label="Fan1Holder"
  AllowCompound = false
  Group = -> [Sketch,Pad,Sketch001,Pad001,Sketch002,AdditivePipe,Sketch003,Pad002,LinearPattern,Sketch004,Pad003,LinearPattern001,FanMountHole,Sketch005,Pocket,OtherFanHolder,FilterHolderMount,Sketch010,Pad008,Sketch011,Pad009,Mount1,Mount2,Sketch031,Pocket008,Sketch032,AdditivePipe002]
  Origin = -> Origin
  Tip = -> AdditivePipe002
FEATURE [App::DocumentObjectGroup] Parts
  Group = -> [Body,Body001,Body002,Body003,Body004]
